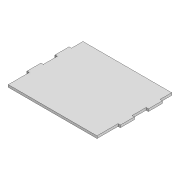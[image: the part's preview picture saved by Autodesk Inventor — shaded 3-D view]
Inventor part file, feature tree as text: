
AUTODESK INVENTOR PART (.ipt)
format: ipt  version: 2022 (Build 260153000, 153)  size: 99,840 bytes
history: native  units: mm
features: extrude x1, sketch x1
ambient origin geometry x8: Origin, YZ Plane, XZ Plane, XY Plane, X Axis, Y Axis, Z Axis, Center Point
bodies: Solid1 (feature_tree)
feature tree (2):
  extrude  "Extrusion1"  Depth=160.0mm
  sketch  "Sketch1"  dims[d0=190.0mm d1=160.0mm d2=5.0mm d3=30.0mm d4=5.0mm d5=30.0mm d6=30.0mm d7=5.0mm d8=5.0mm d9=0.0mm]
